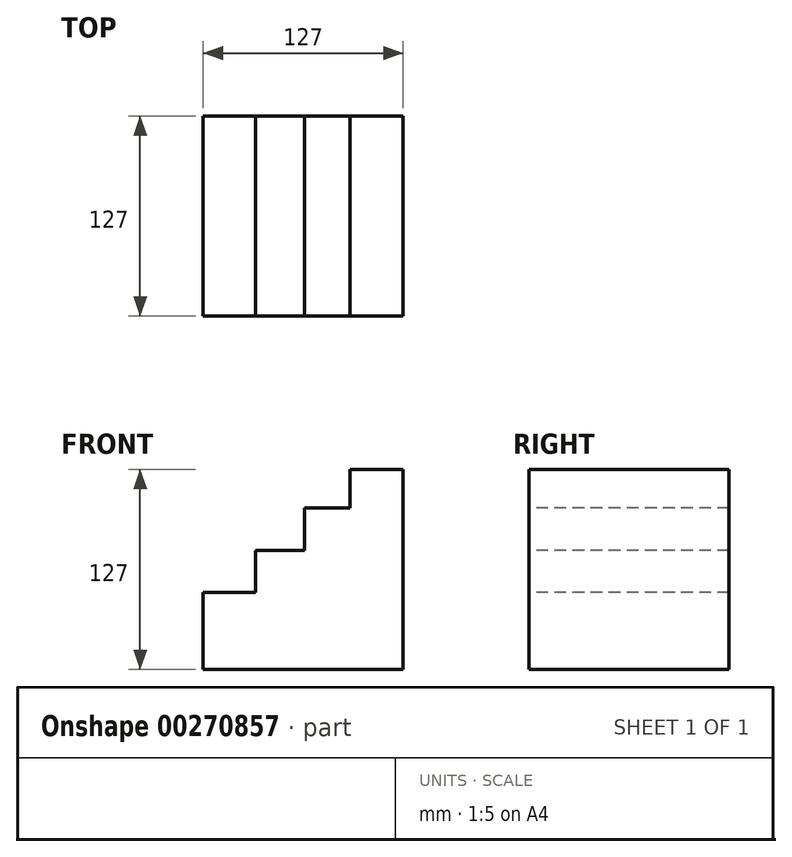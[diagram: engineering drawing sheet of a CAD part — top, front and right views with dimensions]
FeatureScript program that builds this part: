
annotation { "Feature Type Name" : "Feature", "Feature Type Description" : "" }
export const myFeature = defineFeature(function(context is Context, id is Id, definition is map)
    precondition{}
    {
        {
            var Q0;
            Q0=qCreatedBy(makeId("Front.planeOp"),FACE);
            var sketch = newSketch(context, id + "F0", { "sketchPlane" : qUnion([Q0])});
            skLineSegment(sketch, "E0.bottom", {"start": v(-112.3, 110.39) * mm, "end": v(14.7, 110.39) * mm});
            skLineSegment(sketch, "E0.top", {"start": v(-112.3, -16.61) * mm, "end": v(14.7, -16.61) * mm});
            skLineSegment(sketch, "E0.left", {"start": v(-112.3, 110.39) * mm, "end": v(-112.3, -16.61) * mm});
            skLineSegment(sketch, "E0.right", {"start": v(14.7, 110.39) * mm, "end": v(14.7, -16.61) * mm});
            skSolve(sketch);
        }
        {
            var Q0;
            Q0 = qSketchRegion(id + "F0", true);
            extrude(context, id + "F1", {"entities" : qUnion([Q0]), "depth" : 127 * mm});
        }
        {
            var Q0;
            Q0=makeQuery(id+"F1.opExtrude","CAP_FACE",FACE,{"disambiguationData":[OSD([sQuery(id+"F0.wireOp",EDGE,"E0.bottom"),sQuery(id+"F0.wireOp",EDGE,"E0.top"),sQuery(id+"F0.wireOp",EDGE,"E0.left"),sQuery(id+"F0.wireOp",EDGE,"E0.right")])],"isStart":false});
            var sketch = newSketch(context, id + "F2", { "sketchPlane" : qUnion([Q0])});
            skLineSegment(sketch, "E1", {"start": v(-112.3, 32.24) * mm, "end": v(-79.03, 32.24) * mm});
            skLineSegment(sketch, "E2", {"start": v(-79.03, 32.24) * mm, "end": v(-79.03, 59.12) * mm});
            skLineSegment(sketch, "E3", {"start": v(-79.03, 59.12) * mm, "end": v(-48.07, 59.12) * mm});
            skLineSegment(sketch, "E4", {"start": v(-48.07, 59.12) * mm, "end": v(-48.07, 86) * mm});
            skLineSegment(sketch, "E5", {"start": v(-48.07, 86) * mm, "end": v(-19.15, 86) * mm});
            skLineSegment(sketch, "E6", {"start": v(-19.15, 86) * mm, "end": v(-19.15, 110.39) * mm});
            skLineSegment(sketch, "E7", {"start": v(-112.3, 32.24) * mm, "end": v(-112.3, 110.39) * mm});
            skLineSegment(sketch, "E8", {"start": v(-112.3, 110.39) * mm, "end": v(-19.15, 110.39) * mm});
            skSolve(sketch);
        }
        {
            var Q0;
            Q0 = qSketchRegion(id + "F2", true);
            extrude(context, id + "F3", {"entities" : qUnion([Q0]), "operationType" : NewBodyOperationType.REMOVE, "oppositeDirection" : true, "depth" : 127 * mm});
        }
    });
